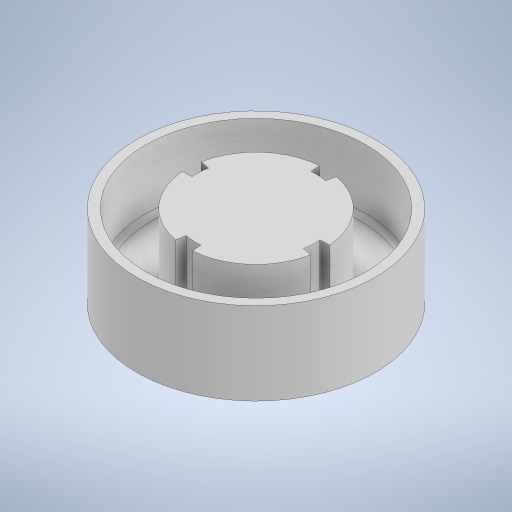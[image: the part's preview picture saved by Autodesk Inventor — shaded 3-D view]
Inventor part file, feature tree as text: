
AUTODESK INVENTOR PART (.ipt)
format: ipt  version: 2023.5 (Build 275446000, 446)  size: 268,288 bytes
history: native  units: mm
features: extrude x3, sketch x2, other x1, fillet x1, projected_geometry x1
ambient origin geometry x8: Origin, YZ Plane, XZ Plane, XY Plane, X Axis, Y Axis, Z Axis, Center Point
bodies: Body1 (feature_tree)
feature tree (8):
  other  "Bryła1"
  sketch  "Szkic1"
  extrude  "Wyciągnięcie proste1"  Depth=24.0mm
  extrude  "Wyciągnięcie proste2"  Depth=1.0mm
  extrude  "Wyciągnięcie proste3"  Depth=7.0mm TaperAngle=0.0deg
  fillet  "Zaokrąglenie1"  Radius=2.0mm
  sketch  "Szkic2"
  projected_geometry  "Pętla rzutowana1"
